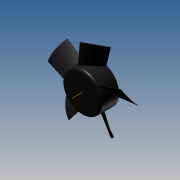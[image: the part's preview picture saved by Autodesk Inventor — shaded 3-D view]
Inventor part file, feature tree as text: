
AUTODESK INVENTOR PART (.ipt)
format: ipt  version: 2014 (Build 180170000, 170)  size: 171,008 bytes
history: native  units: mm (DEFAULTED — no unit token found)
features: sketch x6, extrude x3, plane x3, fillet x1, loft x1, other x1, pattern_circular x1
ambient origin geometry x8: Origin, YZ Plane, XZ Plane, XY Plane, X Axis, Y Axis, Z Axis, Center Point
bodies: Solid1 (feature_tree)
feature tree (16):
  extrude  "Extrusion1"  Depth=26.416mm TaperAngle=0.0deg
  fillet  "Fillet1"  Radius=3.175mm
  sketch  "Sketch2"  dims[d5=38.1mm d6=-12.7mm]
  plane  "Work Plane1"
  plane  "Work Plane2"
  sketch  "Sketch4"  dims[d7=0.0mm d8=90.0deg]
  plane  "Work Plane3"
  loft  "Loft1"
  other  "Work Axis1"
  pattern_circular  "Circular Pattern1"  Count=5 Angle=360.0deg
  extrude  "Extrusion2"  Depth=1.27mm
  extrude  "Extrusion3"  Depth=22.225mm TaperAngle=0.0deg
  sketch  "Sketch1"  dims[d0=57.785mm d1=26.416mm d2=0.0mm d3=3.175mm]
  sketch  "Sketch5"  dims[d9=0.0mm d10=90.0deg]
  sketch  "Sketch6"  dims[d11=114.3mm]
  sketch  "Sketch7"  dims[d12=26.416mm d13=0.0mm d14=50.0mm d16=360.0deg d17=1.27mm d18=22.225mm d19=0.0mm]
